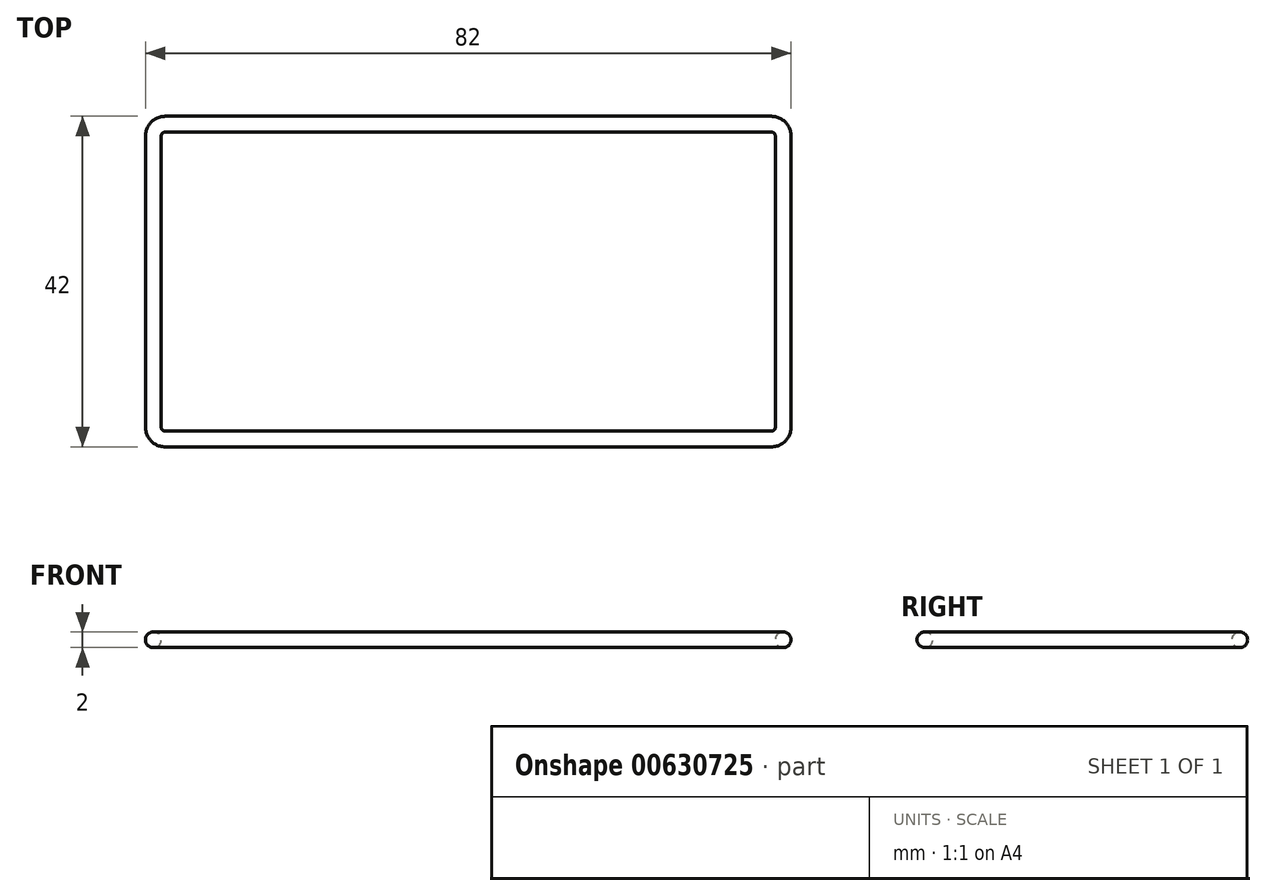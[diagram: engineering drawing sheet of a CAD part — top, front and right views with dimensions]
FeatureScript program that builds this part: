
annotation { "Feature Type Name" : "Feature", "Feature Type Description" : "" }
export const myFeature = defineFeature(function(context is Context, id is Id, definition is map)
    precondition{}
    {
        {
            var Q0;
            Q0=qCreatedBy(makeId("Top.planeOp"),FACE);
            var sketch = newSketch(context, id + "F0", { "sketchPlane" : qUnion([Q0])});
            skLineSegment(sketch, "E0.bottom", {"start": v(38.5, -20) * mm, "end": v(-38.5, -20) * mm});
            skLineSegment(sketch, "E0.top", {"start": v(38.5, 20) * mm, "end": v(-38.5, 20) * mm});
            skLineSegment(sketch, "E0.left", {"start": v(40, -18.5) * mm, "end": v(40, 18.5) * mm});
            skLineSegment(sketch, "E0.right", {"start": v(-40, -18.5) * mm, "end": v(-40, 18.5) * mm});
            skPoint(sketch, "E0.middle", {"position": v(0, 0) * mm});
            skPoint(sketch, "E1.visualSharp", {"position": v(-40, 20) * mm});
            skArc(sketch, "E1.filletArc", {"start": v(-38.5, 20) * mm, "mid": v(-39.56, 19.56) * mm, "end": v(-40, 18.5) * mm});
            skPoint(sketch, "E2.visualSharp", {"position": v(40, 20) * mm});
            skArc(sketch, "E2.filletArc", {"start": v(40, 18.5) * mm, "mid": v(39.56, 19.56) * mm, "end": v(38.5, 20) * mm});
            skPoint(sketch, "E3.visualSharp", {"position": v(40, -20) * mm});
            skArc(sketch, "E3.filletArc", {"start": v(38.5, -20) * mm, "mid": v(39.56, -19.56) * mm, "end": v(40, -18.5) * mm});
            skPoint(sketch, "E4.visualSharp", {"position": v(-40, -20) * mm});
            skArc(sketch, "E4.filletArc", {"start": v(-40, -18.5) * mm, "mid": v(-39.56, -19.56) * mm, "end": v(-38.5, -20) * mm});
            skSolve(sketch);
        }
        {
            var Q0;
            Q0=qCreatedBy(makeId("Right.planeOp"),FACE);
            cPlane(context, id + "F1", {"entities" : qUnion([Q0]), "cplaneType" : CPlaneType.OFFSET, "offset" : 36.5 * mm, "width" : 150 * mm, "height" : 150 * mm});
        }
        {
            var Q0;
            Q0=qCreatedBy(id+"F1.planeOp",FACE);
            var sketch = newSketch(context, id + "F2", { "sketchPlane" : qUnion([Q0])});
            skCircle(sketch, "E5", {"center": v(-20, 0) * mm, "radius": 1 * mm});
            skLineSegment(sketch, "E6", {"start": v(0, 9.77) * mm, "end": v(0, -8.54) * mm, "construction": true});
            skSolve(sketch);
        }
        {
            var Q0;
            Q0=makeQuery(id+"F2.imprint","IMPRINT",FACE,{"disambiguationData":[TD([[makeQuery(id+"F2.imprint","IMPRINT",EDGE,{"derivedFrom":sQuery(id+"F2.wireOp",EDGE,"E5")}),1.0]])]});
            var Q1;
            Q1=sQuery(id+"F0.wireOp",EDGE,"E0.bottom");
            var Q2;
            Q2=sQuery(id+"F0.wireOp",EDGE,"E4.filletArc");
            var Q3;
            Q3=sQuery(id+"F0.wireOp",EDGE,"E0.right");
            var Q4;
            Q4=sQuery(id+"F0.wireOp",EDGE,"E1.filletArc");
            var Q5;
            Q5=sQuery(id+"F0.wireOp",EDGE,"E0.top");
            var Q6;
            Q6=sQuery(id+"F0.wireOp",EDGE,"E2.filletArc");
            var Q7;
            Q7=sQuery(id+"F0.wireOp",EDGE,"E0.left");
            var Q8;
            Q8=sQuery(id+"F0.wireOp",EDGE,"E3.filletArc");
            sweep(context, id + "F3", {"profiles" : qUnion([Q0]), "path" : qUnion([Q1, Q2, Q3, Q4, Q5, Q6, Q7, Q8])});
        }
    });
